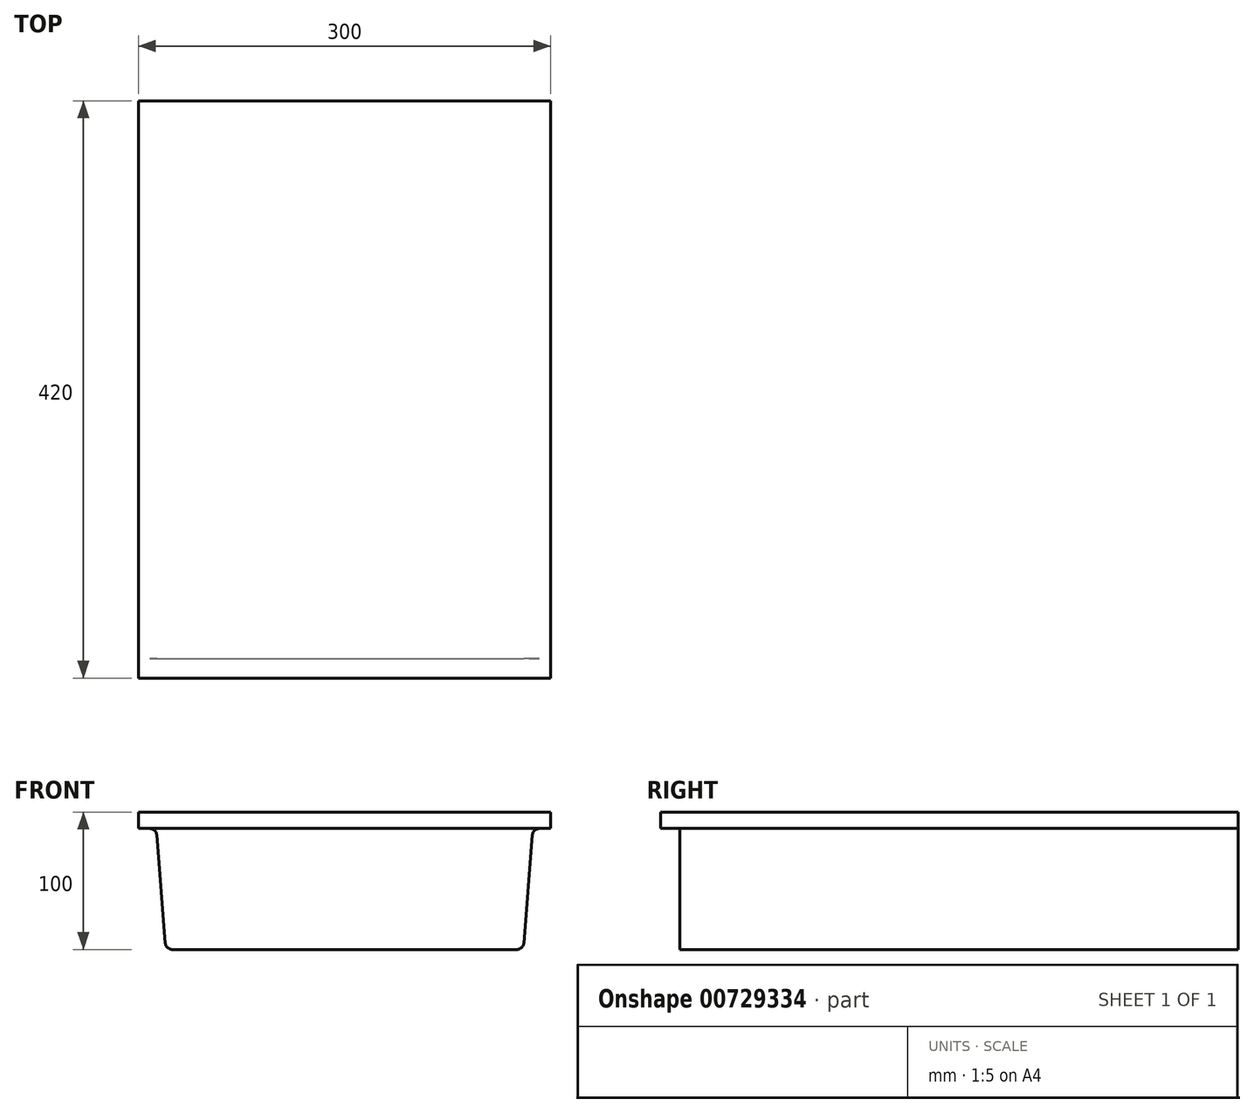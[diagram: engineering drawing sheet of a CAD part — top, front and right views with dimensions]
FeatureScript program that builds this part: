
annotation { "Feature Type Name" : "Feature", "Feature Type Description" : "" }
export const myFeature = defineFeature(function(context is Context, id is Id, definition is map)
    precondition{}
    {
        {
            var Q0;
            Q0=qCreatedBy(makeId("Front.planeOp"),FACE);
            var sketch = newSketch(context, id + "F0", { "sketchPlane" : qUnion([Q0])});
            skLineSegment(sketch, "E0", {"start": v(0, 0) * mm, "end": v(-150, 0) * mm});
            skLineSegment(sketch, "E1", {"start": v(-150, 0) * mm, "end": v(-150, -12) * mm});
            skLineSegment(sketch, "E2", {"start": v(-150, -12) * mm, "end": v(-141.62, -12) * mm});
            skLineSegment(sketch, "E3", {"start": v(-136.63, -16.6) * mm, "end": v(-130.37, -95.4) * mm});
            skLineSegment(sketch, "E4", {"start": v(-125.38, -100) * mm, "end": v(0, -100) * mm});
            skLineSegment(sketch, "E5.MirrorCS", {"start": v(150, -12) * mm, "end": v(141.62, -12) * mm});
            skLineSegment(sketch, "E6.MirrorCS", {"start": v(150, 0) * mm, "end": v(150, -12) * mm});
            skLineSegment(sketch, "E7.MirrorCS", {"start": v(136.63, -16.6) * mm, "end": v(130.37, -95.4) * mm});
            skLineSegment(sketch, "E8.MirrorCS", {"start": v(125.38, -100) * mm, "end": v(0, -100) * mm});
            skLineSegment(sketch, "E9.MirrorCS", {"start": v(0, 0) * mm, "end": v(150, 0) * mm});
            skPoint(sketch, "E10.visualSharp", {"position": v(-137, -12) * mm});
            skArc(sketch, "E10.filletArc", {"start": v(-136.63, -16.6) * mm, "mid": v(-138.23, -13.33) * mm, "end": v(-141.62, -12) * mm});
            skPoint(sketch, "E11.visualSharp", {"position": v(-130, -100) * mm});
            skArc(sketch, "E11.filletArc", {"start": v(-130.37, -95.4) * mm, "mid": v(-128.77, -98.67) * mm, "end": v(-125.38, -100) * mm});
            skPoint(sketch, "E12.visualSharp", {"position": v(130, -100) * mm});
            skArc(sketch, "E12.filletArc", {"start": v(125.38, -100) * mm, "mid": v(128.77, -98.67) * mm, "end": v(130.37, -95.4) * mm});
            skPoint(sketch, "E13.visualSharp", {"position": v(137, -12) * mm});
            skArc(sketch, "E13.filletArc", {"start": v(141.62, -12) * mm, "mid": v(138.23, -13.33) * mm, "end": v(136.63, -16.6) * mm});
            skSolve(sketch);
        }
        {
            var Q0;
            Q0=makeQuery(id+"F0.imprint","IMPRINT",FACE,{"disambiguationData":[TD([[makeQuery(id+"F0.imprint","IMPRINT",EDGE,{"derivedFrom":sQuery(id+"F0.wireOp",EDGE,"E0")}),1.0]])]});
            extrude(context, id + "F1", {"entities" : qUnion([Q0]), "depth" : 420 * mm, "offsetDistance" : 25 * mm});
        }
        {
            var Q0;
            Q0=makeQuery(id+"F1.opExtrude","CAP_FACE",FACE,{"disambiguationData":[OSD([sQuery(id+"F0.wireOp",EDGE,"E0"),sQuery(id+"F0.wireOp",EDGE,"E1"),sQuery(id+"F0.wireOp",EDGE,"E2"),sQuery(id+"F0.wireOp",EDGE,"E3"),sQuery(id+"F0.wireOp",EDGE,"E4"),sQuery(id+"F0.wireOp",EDGE,"E5.MirrorCS"),sQuery(id+"F0.wireOp",EDGE,"E6.MirrorCS"),sQuery(id+"F0.wireOp",EDGE,"E7.MirrorCS"),sQuery(id+"F0.wireOp",EDGE,"E8.MirrorCS"),sQuery(id+"F0.wireOp",EDGE,"E9.MirrorCS"),sQuery(id+"F0.wireOp",EDGE,"E10.filletArc"),sQuery(id+"F0.wireOp",EDGE,"E11.filletArc"),sQuery(id+"F0.wireOp",EDGE,"E12.filletArc"),sQuery(id+"F0.wireOp",EDGE,"E13.filletArc")])],"isStart":false});
            var sketch = newSketch(context, id + "F2", { "sketchPlane" : qUnion([Q0])});
            skLineSegment(sketch, "E14", {"start": v(-141.62, -12) * mm, "end": v(141.62, -12) * mm});
            skSolve(sketch);
        }
        {
            var Q0;
            Q0=makeQuery(id+"F2.imprint","IMPRINT",FACE,{"disambiguationData":[TD([[makeQuery(id+"F2.imprint","IMPRINT",EDGE,{"derivedFrom":sQuery(id+"F2.wireOp",EDGE,"E14")}),-1.0]])]});
            extrude(context, id + "F3", {"entities" : qUnion([Q0]), "operationType" : NewBodyOperationType.REMOVE, "oppositeDirection" : true, "depth" : 14 * mm, "offsetDistance" : 25 * mm});
        }
        {
            var Q0;
            Q0=qCreatedBy(makeId("Front.planeOp"),FACE);
            cPlane(context, id + "F4", {"entities" : qUnion([Q0]), "cplaneType" : CPlaneType.OFFSET, "offset" : 210 * mm, "width" : 150 * mm, "height" : 150 * mm});
        }
    });
